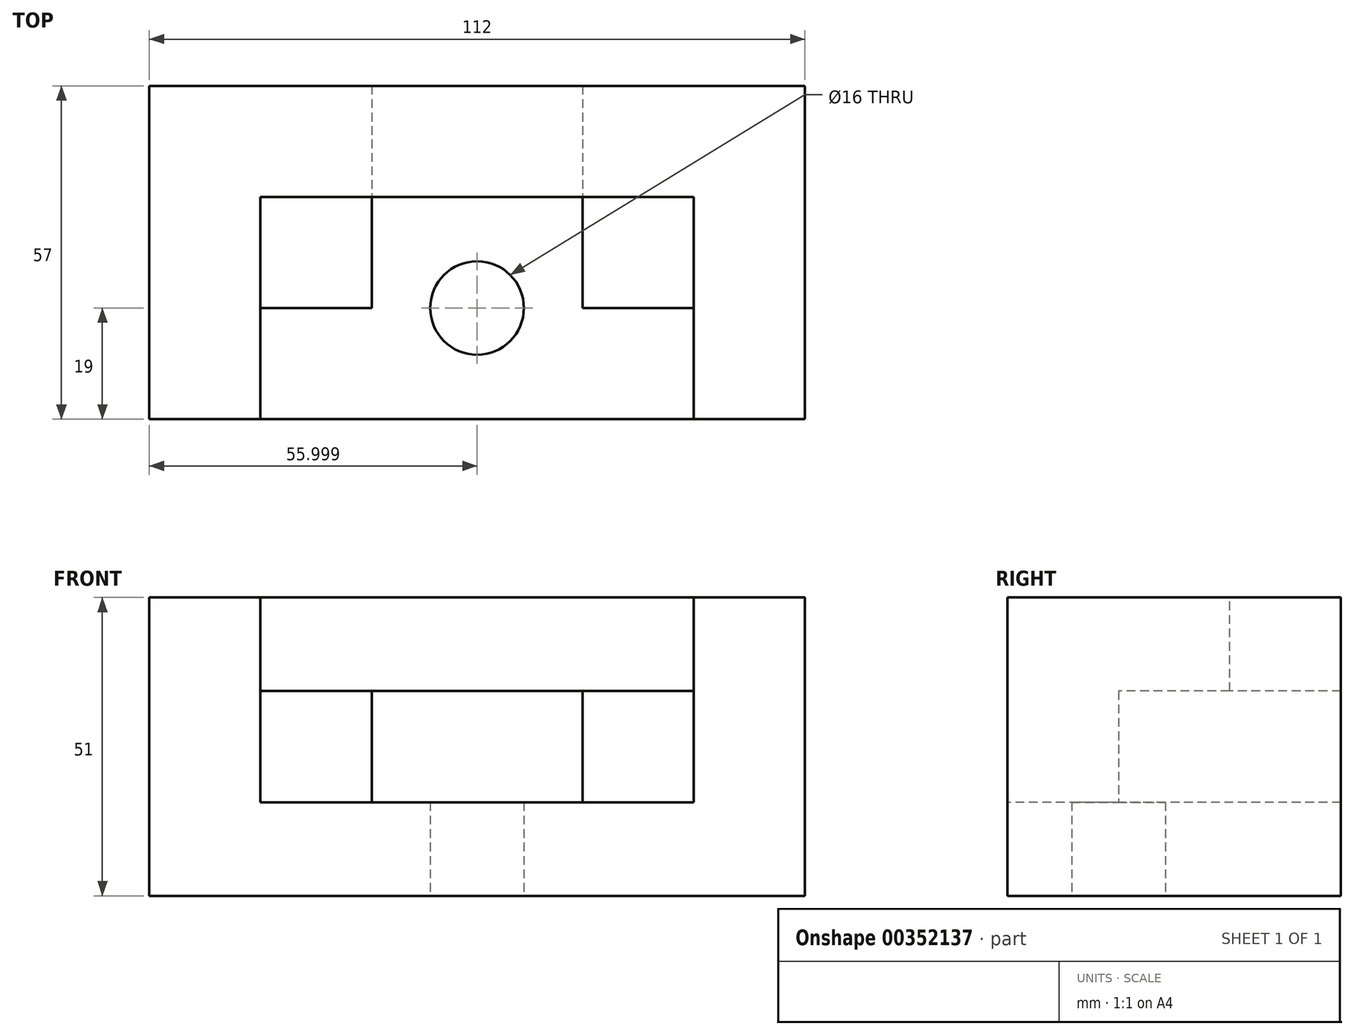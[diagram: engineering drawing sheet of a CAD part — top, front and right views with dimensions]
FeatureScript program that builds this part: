
annotation { "Feature Type Name" : "Feature", "Feature Type Description" : "" }
export const myFeature = defineFeature(function(context is Context, id is Id, definition is map)
    precondition{}
    {
        {
            var Q0;
            Q0=qCreatedBy(makeId("Front.planeOp"),FACE);
            var sketch = newSketch(context, id + "F0", { "sketchPlane" : qUnion([Q0])});
            skLineSegment(sketch, "E0", {"start": v(-50.57, 0) * mm, "end": v(61.43, 0) * mm});
            skLineSegment(sketch, "E1", {"start": v(61.43, 0) * mm, "end": v(61.43, 51) * mm});
            skLineSegment(sketch, "E2", {"start": v(-50.57, 0) * mm, "end": v(-50.57, 51) * mm});
            skLineSegment(sketch, "E3", {"start": v(-50.57, 51) * mm, "end": v(61.43, 51) * mm});
            skSolve(sketch);
        }
        {
            var Q0;
            Q0 = qSketchRegion(id + "F0", true);
            extrude(context, id + "F1", {"entities" : qUnion([Q0]), "depth" : 57 * mm});
        }
        {
            var Q0;
            Q0=makeQuery(id+"F1.opExtrude","CAP_FACE",FACE,{"disambiguationData":[OSD([sQuery(id+"F0.wireOp",EDGE,"E0"),sQuery(id+"F0.wireOp",EDGE,"E1"),sQuery(id+"F0.wireOp",EDGE,"E2"),sQuery(id+"F0.wireOp",EDGE,"E3")])],"isStart":false});
            var sketch = newSketch(context, id + "F2", { "sketchPlane" : qUnion([Q0])});
            skLineSegment(sketch, "E4", {"start": v(-31.57, 51) * mm, "end": v(-31.57, 16) * mm});
            skLineSegment(sketch, "E5", {"start": v(-31.57, 16) * mm, "end": v(42.43, 16) * mm});
            skLineSegment(sketch, "E6", {"start": v(42.43, 16) * mm, "end": v(42.43, 51) * mm});
            skSolve(sketch);
        }
        {
            var Q0;
            Q0 = qSketchRegion(id + "F2", true);
            var Q1;
            {var subQ0=sQuery(id+"F2.wireOp",EDGE,"E4");Q1=makeQuery(id+"F2.imprint","IMPRINT",FACE,{"disambiguationData":[TD([[makeQuery(id+"F2.imprint","IMPRINT",EDGE,{"derivedFrom":subQ0}),1.0]])]});}
            extrude(context, id + "F3", {"entities" : qUnion([Q0, Q1]), "operationType" : NewBodyOperationType.REMOVE, "oppositeDirection" : true, "depth" : 19 * mm});
        }
        {
            var Q0;
            Q0=makeQuery(id+"F1.opExtrude","SWEPT_FACE",FACE,{"disambiguationData":[OSD([sQuery(id+"F0.wireOp",EDGE,"E3")])]});
            var sketch = newSketch(context, id + "F4", { "sketchPlane" : qUnion([Q0])});
            skLineSegment(sketch, "E7", {"start": v(-31.57, -38) * mm, "end": v(-31.57, -19) * mm});
            skLineSegment(sketch, "E8", {"start": v(-31.57, -19) * mm, "end": v(42.43, -19) * mm});
            skLineSegment(sketch, "E9", {"start": v(42.43, -19) * mm, "end": v(42.43, -38) * mm});
            skSolve(sketch);
        }
        {
            var Q0;
            Q0 = qSketchRegion(id + "F4", true);
            var Q1;
            Q1=makeQuery(id+"F4.imprint","IMPRINT",FACE,{"disambiguationData":[TD([[makeQuery(id+"F4.imprint","IMPRINT",EDGE,{"derivedFrom":sQuery(id+"F4.wireOp",EDGE,"E7")}),-1.0]])]});
            extrude(context, id + "F5", {"entities" : qUnion([Q0, Q1]), "operationType" : NewBodyOperationType.REMOVE, "oppositeDirection" : true, "depth" : 16 * mm});
        }
        {
            var Q0;
            Q0=makeQuery(id+"F3.boolean.opBoolean","COPY",FACE,{"derivedFrom":makeQuery(id+"F3.opExtrude","CAP_FACE",FACE,{"disambiguationData":[OSD([sQuery(id+"F0.wireOp",EDGE,"E3"),sQuery(id+"F2.wireOp",EDGE,"E4"),sQuery(id+"F2.wireOp",EDGE,"E5"),sQuery(id+"F2.wireOp",EDGE,"E6")])],"isStart":false})});
            var sketch = newSketch(context, id + "F6", { "sketchPlane" : qUnion([Q0])});
            skLineSegment(sketch, "E10", {"start": v(23.43, 35) * mm, "end": v(23.43, 16) * mm});
            skLineSegment(sketch, "E11", {"start": v(23.43, 16) * mm, "end": v(42.43, 16) * mm});
            skLineSegment(sketch, "E12", {"start": v(42.43, 16) * mm, "end": v(42.43, 35) * mm});
            skLineSegment(sketch, "E13", {"start": v(42.43, 35) * mm, "end": v(23.43, 35) * mm});
            skLineSegment(sketch, "E14", {"start": v(-12.57, 35) * mm, "end": v(-12.57, 16) * mm});
            skLineSegment(sketch, "E15", {"start": v(-12.57, 16) * mm, "end": v(-31.57, 16) * mm});
            skLineSegment(sketch, "E16", {"start": v(-31.57, 16) * mm, "end": v(-31.57, 35) * mm});
            skLineSegment(sketch, "E17", {"start": v(-31.57, 35) * mm, "end": v(-12.57, 35) * mm});
            skSolve(sketch);
        }
        {
            var Q0;
            {var subQ0=sQuery(id+"F6.wireOp",EDGE,"E10");Q0=makeQuery(id+"F6.imprint","IMPRINT",FACE,{"disambiguationData":[TD([[makeQuery(id+"F6.imprint","IMPRINT",EDGE,{"derivedFrom":subQ0}),-1.0]])]});}
            extrude(context, id + "F7", {"entities" : qUnion([Q0]), "operationType" : NewBodyOperationType.REMOVE, "endBound" : BoundingType.THROUGH_ALL, "oppositeDirection" : true, "depth" : 25 * mm});
        }
        {
            var Q0;
            Q0=makeQuery(id+"F1.opExtrude","SWEPT_FACE",FACE,{"disambiguationData":[OSD([sQuery(id+"F0.wireOp",EDGE,"E0")])]});
            var sketch = newSketch(context, id + "F8", { "sketchPlane" : qUnion([Q0])});
            skPoint(sketch, "E18", {"position": v(5.43, 38) * mm});
            skCircle(sketch, "E19", {"center": v(5.43, 38) * mm, "radius": 8 * mm});
            skSolve(sketch);
        }
        {
            var Q0;
            Q0 = qSketchRegion(id + "F8", true);
            extrude(context, id + "F9", {"entities" : qUnion([Q0]), "operationType" : NewBodyOperationType.REMOVE, "oppositeDirection" : true, "depth" : 16 * mm});
        }
    });
